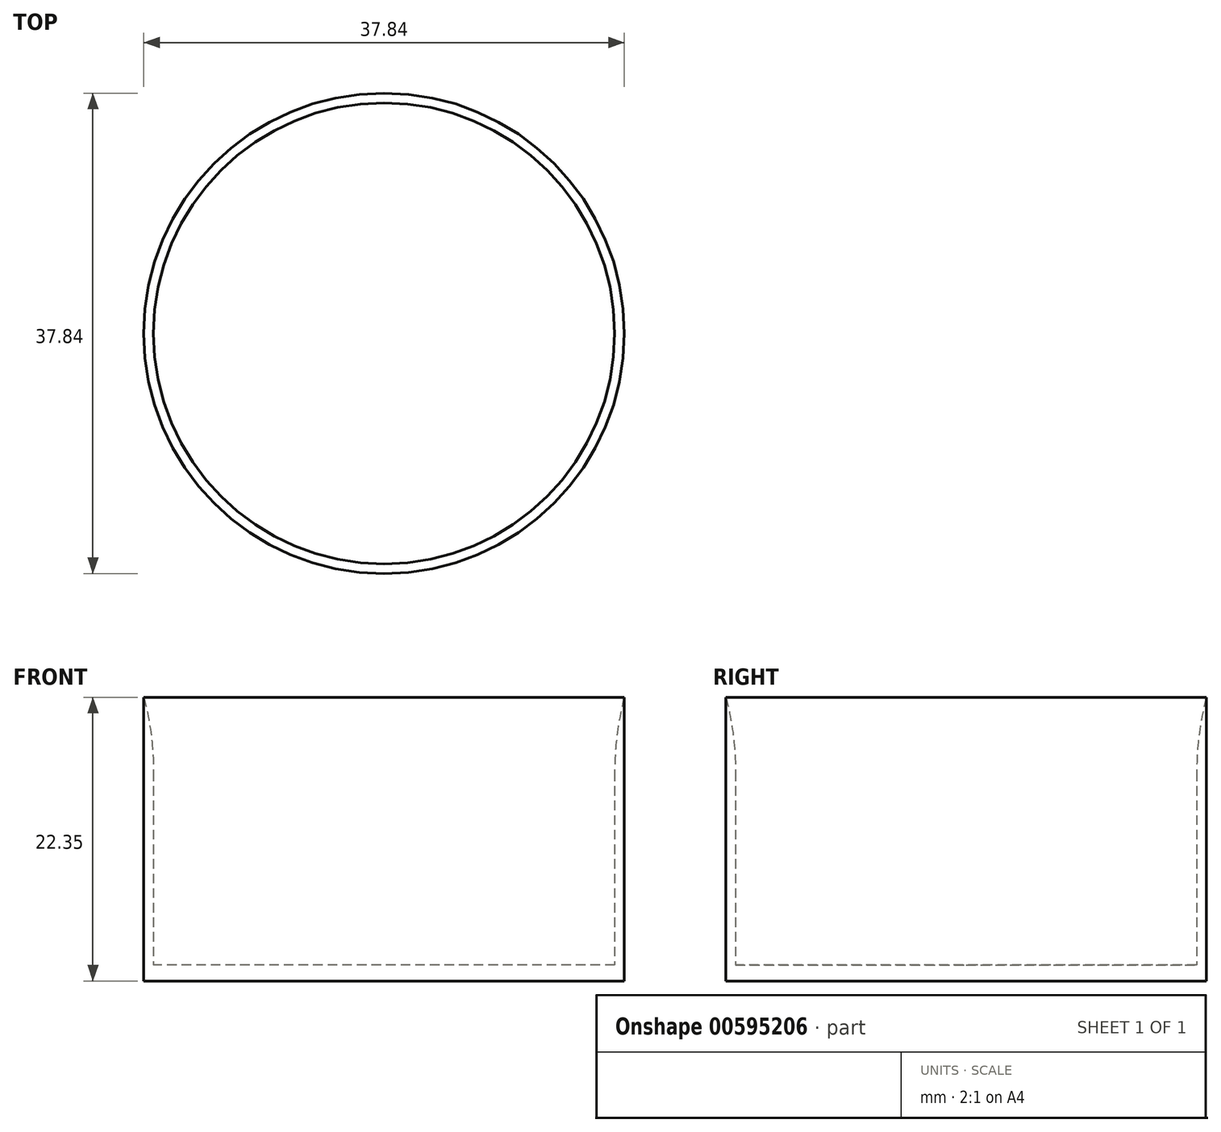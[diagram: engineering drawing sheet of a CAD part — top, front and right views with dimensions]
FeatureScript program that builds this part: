
annotation { "Feature Type Name" : "Feature", "Feature Type Description" : "" }
export const myFeature = defineFeature(function(context is Context, id is Id, definition is map)
    precondition{}
    {
        {
            var Q0;
            Q0=qCreatedBy(makeId("Top.planeOp"),FACE);
            var sketch = newSketch(context, id + "F0", { "sketchPlane" : qUnion([Q0])});
            skCircle(sketch, "E0", {"center": v(0, 0) * mm, "radius": 18.16 * mm});
            skCircle(sketch, "E1.0", {"center": v(0, 0) * mm, "radius": 18.92 * mm});
            skSolve(sketch);
        }
        {
            var Q0;
            Q0 = qSketchRegion(id + "F0", true);
            extrude(context, id + "F1", {"entities" : qUnion([Q0]), "depth" : 22.35 * mm, "offsetDistance" : 25.4 * mm});
        }
        {
            var Q0;
            Q0=qCreatedBy(makeId("Top.planeOp"),FACE);
            var sketch = newSketch(context, id + "F2", { "sketchPlane" : qUnion([Q0])});
            skCircle(sketch, "E2", {"center": v(0, 0) * mm, "radius": 18.88 * mm});
            skSolve(sketch);
        }
        {
            var Q0;
            Q0 = qSketchRegion(id + "F2", true);
            extrude(context, id + "F3", {"entities" : qUnion([Q0]), "operationType" : NewBodyOperationType.ADD, "depth" : 1.27 * mm, "offsetDistance" : 25.4 * mm});
        }
        {
            var Q0;
            Q0=makeQuery(id+"F1.opExtrude","CAP_EDGE",EDGE,{"disambiguationData":[OSD([sQuery(id+"F0.wireOp",EDGE,"E0")])],"isStart":false});
            fillet(context, id + "F4", {"entities" : qUnion([Q0]), "radius" : 22.86 * mm, "tangentPropagation" : true, "allowEdgeOverflow" : false});
        }
    });
